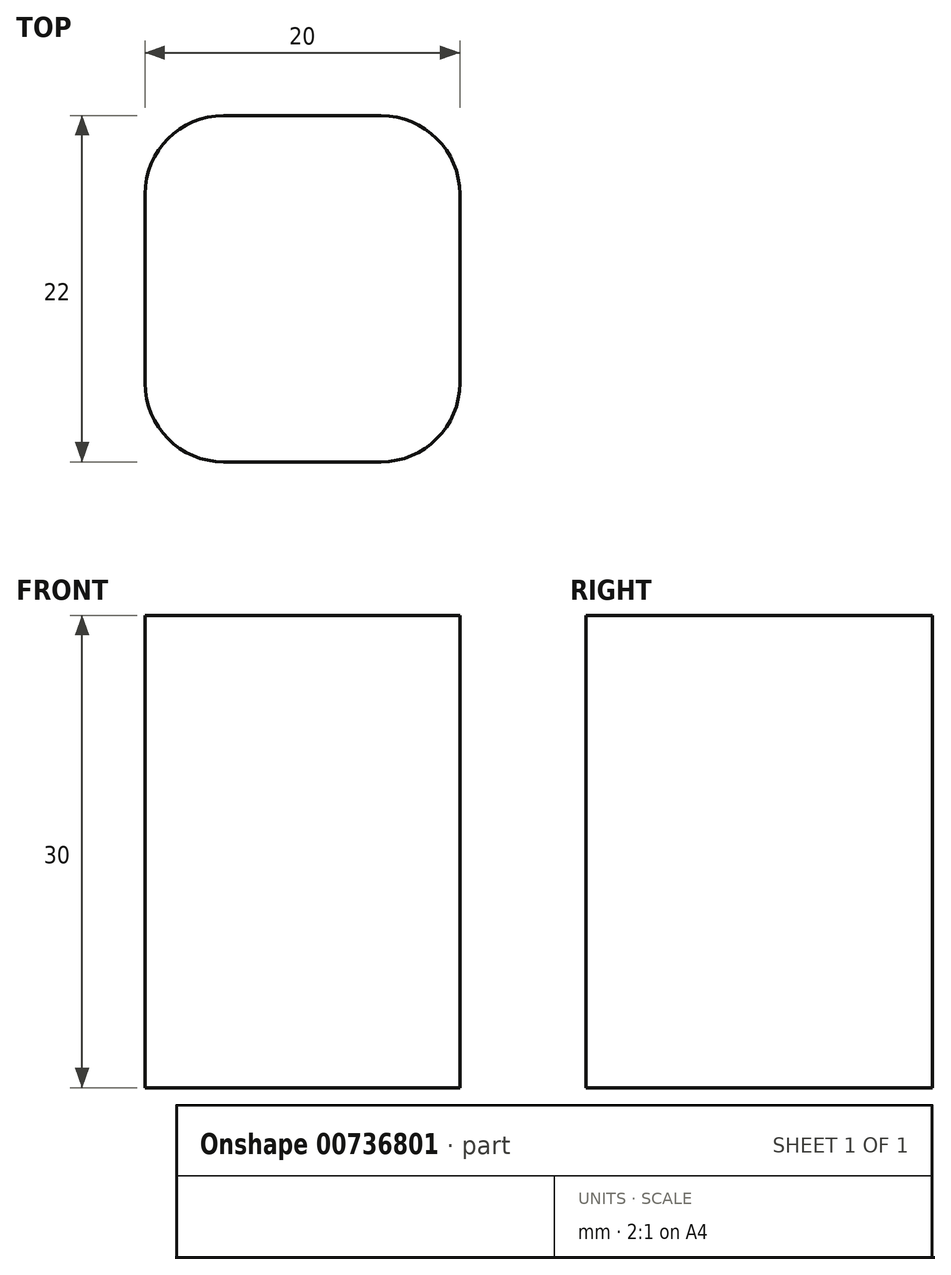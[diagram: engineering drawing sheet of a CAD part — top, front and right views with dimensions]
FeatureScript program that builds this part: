
annotation { "Feature Type Name" : "Feature", "Feature Type Description" : "" }
export const myFeature = defineFeature(function(context is Context, id is Id, definition is map)
    precondition{}
    {
        {
            var Q0;
            Q0=qCreatedBy(makeId("Top.planeOp"),FACE);
            var sketch = newSketch(context, id + "F0", { "sketchPlane" : qUnion([Q0])});
            skLineSegment(sketch, "E0", {"start": v(-19.07, 22) * mm, "end": v(0.93, 22) * mm});
            skLineSegment(sketch, "E1", {"start": v(0.93, 22) * mm, "end": v(0.93, 0) * mm});
            skLineSegment(sketch, "E2", {"start": v(0.93, 0) * mm, "end": v(-19.07, 0) * mm});
            skLineSegment(sketch, "E3", {"start": v(-19.07, 0) * mm, "end": v(-19.07, 22) * mm});
            skSolve(sketch);
        }
        {
            var Q0;
            Q0=makeQuery(id+"F0.imprint","IMPRINT",FACE,{"disambiguationData":[TD([[makeQuery(id+"F0.imprint","IMPRINT",EDGE,{"derivedFrom":sQuery(id+"F0.wireOp",EDGE,"E0")}),-1.0]])]});
            extrude(context, id + "F1", {"entities" : qUnion([Q0]), "depth" : 30 * mm, "offsetDistance" : 25 * mm});
        }
        {
            var Q0;
            Q0=makeQuery(id+"F1.opExtrude","SWEPT_EDGE",EDGE,{"disambiguationData":[OSD([sQuery(id+"F0.wireOp",EDGE,"E2"),sQuery(id+"F0.wireOp",EDGE,"E3")])]});
            var Q1;
            Q1=makeQuery(id+"F1.opExtrude","SWEPT_EDGE",EDGE,{"disambiguationData":[OSD([sQuery(id+"F0.wireOp",EDGE,"E1"),sQuery(id+"F0.wireOp",EDGE,"E2")])]});
            var Q2;
            Q2=makeQuery(id+"F1.opExtrude","SWEPT_EDGE",EDGE,{"disambiguationData":[OSD([sQuery(id+"F0.wireOp",EDGE,"E0"),sQuery(id+"F0.wireOp",EDGE,"E1")])]});
            var Q3;
            Q3=makeQuery(id+"F1.opExtrude","SWEPT_EDGE",EDGE,{"disambiguationData":[OSD([sQuery(id+"F0.wireOp",EDGE,"E0"),sQuery(id+"F0.wireOp",EDGE,"E3")])]});
            fillet(context, id + "F2", {"entities" : qUnion([Q0, Q1, Q2, Q3]), "radius" : 5 * mm, "tangentPropagation" : true, "allowEdgeOverflow" : false});
        }
    });
